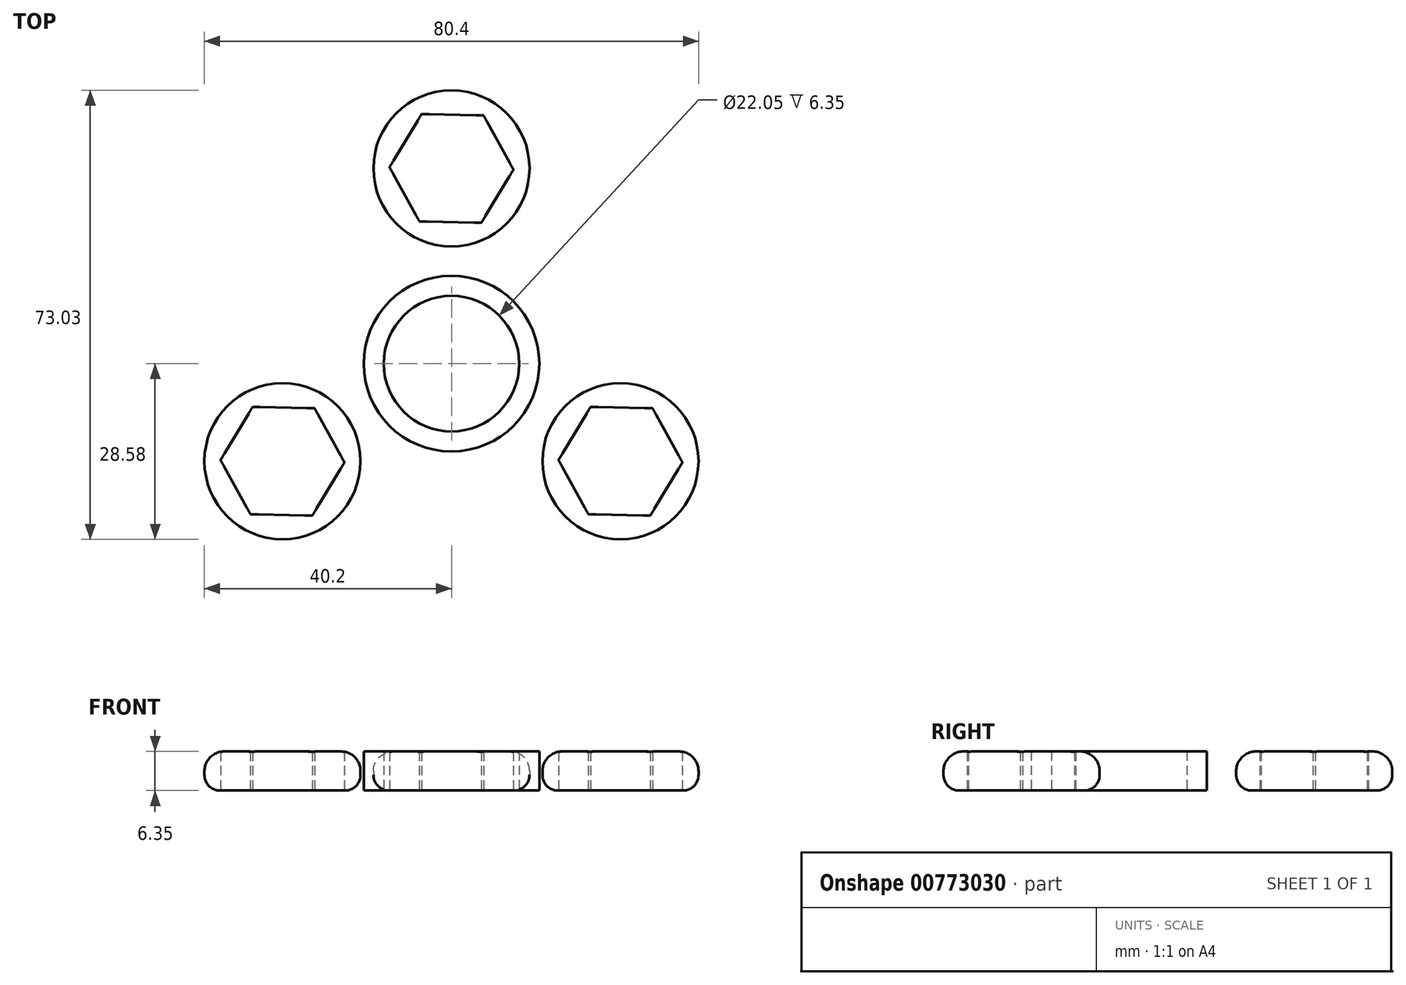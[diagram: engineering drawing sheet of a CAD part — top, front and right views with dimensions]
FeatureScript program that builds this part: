
annotation { "Feature Type Name" : "Feature", "Feature Type Description" : "" }
export const myFeature = defineFeature(function(context is Context, id is Id, definition is map)
    precondition{}
    {
        {
            var Q0;
            Q0=qCreatedBy(makeId("Top.planeOp"),FACE);
            var sketch = newSketch(context, id + "F0", { "sketchPlane" : qUnion([Q0])});
            skCircle(sketch, "E0", {"center": v(0, 0) * mm, "radius": 14.29 * mm});
            skCircle(sketch, "E1", {"center": v(0, 0) * mm, "radius": 11.02 * mm});
            skCircle(sketch, "E2.cCircle", {"center": v(0, 31.75) * mm, "radius": 8.73 * mm, "construction": true});
            skLineSegment(sketch, "E2.0", {"start": v(5.2, 40.38) * mm, "end": v(10.08, 31.55) * mm});
            skLineSegment(sketch, "E2.1", {"start": v(10.08, 31.55) * mm, "end": v(4.87, 22.92) * mm});
            skLineSegment(sketch, "E2.2", {"start": v(4.87, 22.92) * mm, "end": v(-5.2, 23.12) * mm});
            skLineSegment(sketch, "E2.3", {"start": v(-5.2, 23.12) * mm, "end": v(-10.08, 31.95) * mm});
            skLineSegment(sketch, "E2.4", {"start": v(-10.08, 31.95) * mm, "end": v(-4.87, 40.58) * mm});
            skLineSegment(sketch, "E2.5", {"start": v(-4.87, 40.58) * mm, "end": v(5.2, 40.38) * mm});
            skPoint(sketch, "E2.0.midPoint", {"position": v(7.64, 35.97) * mm});
            skCircle(sketch, "E3", {"center": v(0, 31.75) * mm, "radius": 12.7 * mm});
            skCircle(sketch, "E4.1.0", {"center": v(-27.5, -15.87) * mm, "radius": 8.73 * mm, "construction": true});
            skLineSegment(sketch, "E4.1.1", {"start": v(-22.29, -7.24) * mm, "end": v(-17.42, -16.07) * mm});
            skCircle(sketch, "E4.1.2", {"center": v(-27.5, -15.87) * mm, "radius": 12.7 * mm});
            skPoint(sketch, "E4.1.3", {"position": v(-34.97, -11.36) * mm});
            skLineSegment(sketch, "E4.1.4", {"start": v(-32.37, -7.05) * mm, "end": v(-22.29, -7.24) * mm});
            skLineSegment(sketch, "E4.1.5", {"start": v(-17.42, -16.07) * mm, "end": v(-22.63, -24.7) * mm});
            skLineSegment(sketch, "E4.1.6", {"start": v(-32.7, -24.5) * mm, "end": v(-37.58, -15.68) * mm});
            skLineSegment(sketch, "E4.1.7", {"start": v(-37.58, -15.68) * mm, "end": v(-32.37, -7.05) * mm});
            skLineSegment(sketch, "E4.1.8", {"start": v(-22.63, -24.7) * mm, "end": v(-32.7, -24.5) * mm});
            skCircle(sketch, "E4.2.0", {"center": v(27.5, -15.87) * mm, "radius": 8.73 * mm, "construction": true});
            skLineSegment(sketch, "E4.2.1", {"start": v(17.42, -15.68) * mm, "end": v(22.63, -7.05) * mm});
            skCircle(sketch, "E4.2.2", {"center": v(27.5, -15.87) * mm, "radius": 12.7 * mm});
            skPoint(sketch, "E4.2.3", {"position": v(27.33, -24.6) * mm});
            skLineSegment(sketch, "E4.2.4", {"start": v(22.29, -24.5) * mm, "end": v(17.42, -15.68) * mm});
            skLineSegment(sketch, "E4.2.5", {"start": v(22.63, -7.05) * mm, "end": v(32.7, -7.24) * mm});
            skLineSegment(sketch, "E4.2.6", {"start": v(37.58, -16.07) * mm, "end": v(32.37, -24.7) * mm});
            skLineSegment(sketch, "E4.2.7", {"start": v(32.37, -24.7) * mm, "end": v(22.29, -24.5) * mm});
            skLineSegment(sketch, "E4.2.8", {"start": v(32.7, -7.24) * mm, "end": v(37.58, -16.07) * mm});
            skSolve(sketch);
        }
        {
            var Q0;
            Q0=qCreatedBy(makeId("Top.planeOp"),FACE);
            var sketch = newSketch(context, id + "F1", { "sketchPlane" : qUnion([Q0])});
            skCircle(sketch, "E5.0", {"center": v(27.5, -15.87) * mm, "radius": 8.73 * mm});
            skCircle(sketch, "E5.1", {"center": v(27.5, -15.87) * mm, "radius": 12.7 * mm});
            skLineSegment(sketch, "E5.2", {"start": v(22.63, -7.05) * mm, "end": v(32.7, -7.24) * mm});
            skLineSegment(sketch, "E5.3", {"start": v(37.58, -16.07) * mm, "end": v(32.37, -24.7) * mm});
            skLineSegment(sketch, "E5.4", {"start": v(32.7, -7.24) * mm, "end": v(37.58, -16.07) * mm});
            skLineSegment(sketch, "E5.5", {"start": v(-22.29, -7.24) * mm, "end": v(-17.42, -16.07) * mm});
            skCircle(sketch, "E5.6", {"center": v(0, 31.75) * mm, "radius": 12.7 * mm});
            skLineSegment(sketch, "E5.7", {"start": v(-4.87, 40.58) * mm, "end": v(5.2, 40.38) * mm});
            skLineSegment(sketch, "E5.8", {"start": v(-10.08, 31.95) * mm, "end": v(-4.87, 40.58) * mm});
            skLineSegment(sketch, "E5.9", {"start": v(-5.2, 23.12) * mm, "end": v(-10.08, 31.95) * mm});
            skLineSegment(sketch, "E5.10", {"start": v(4.87, 22.92) * mm, "end": v(-5.2, 23.12) * mm});
            skLineSegment(sketch, "E5.11", {"start": v(10.08, 31.55) * mm, "end": v(4.87, 22.92) * mm});
            skCircle(sketch, "E5.12", {"center": v(0, 31.75) * mm, "radius": 8.73 * mm});
            skCircle(sketch, "E5.13", {"center": v(0, 0) * mm, "radius": 11.02 * mm});
            skCircle(sketch, "E5.14", {"center": v(0, 0) * mm, "radius": 14.29 * mm});
            skLineSegment(sketch, "E5.15", {"start": v(-17.42, -16.07) * mm, "end": v(-22.63, -24.7) * mm});
            skLineSegment(sketch, "E5.16", {"start": v(-22.63, -24.7) * mm, "end": v(-32.7, -24.5) * mm});
            skLineSegment(sketch, "E5.17", {"start": v(-32.37, -7.05) * mm, "end": v(-22.29, -7.24) * mm});
            skLineSegment(sketch, "E5.18", {"start": v(17.42, -15.68) * mm, "end": v(22.63, -7.05) * mm});
            skLineSegment(sketch, "E5.19", {"start": v(22.29, -24.5) * mm, "end": v(17.42, -15.68) * mm});
            skLineSegment(sketch, "E5.20", {"start": v(5.2, 40.38) * mm, "end": v(10.08, 31.55) * mm});
            skCircle(sketch, "E6.0", {"center": v(-27.5, -15.87) * mm, "radius": 12.7 * mm});
            skLineSegment(sketch, "E6.1", {"start": v(-32.7, -24.5) * mm, "end": v(-37.58, -15.68) * mm});
            skCircle(sketch, "E6.8", {"center": v(-27.5, -15.87) * mm, "radius": 8.73 * mm});
            skLineSegment(sketch, "E6.23", {"start": v(32.37, -24.7) * mm, "end": v(22.29, -24.5) * mm});
            skSolve(sketch);
        }
        {
            var Q0;
            Q0=qCreatedBy(makeId("Top.planeOp"),FACE);
            var sketch = newSketch(context, id + "F2", { "sketchPlane" : qUnion([Q0])});
            skArc(sketch, "E7.0", {"start": v(-24.29, -3.59) * mm, "mid": v(-38.47, -22.27) * mm, "end": v(-15.23, -19.15) * mm});
            skCircle(sketch, "E7.1", {"center": v(0, 31.75) * mm, "radius": 8.73 * mm});
            skArc(sketch, "E7.2", {"start": v(9.04, 22.83) * mm, "mid": v(-0.05, 44.45) * mm, "end": v(-8.97, 22.76) * mm});
            skArc(sketch, "E7.3", {"start": v(15.25, -19.24) * mm, "mid": v(38.52, -22.18) * mm, "end": v(24.2, -3.61) * mm});
            skCircle(sketch, "E7.4", {"center": v(27.5, -15.87) * mm, "radius": 8.73 * mm});
            skCircle(sketch, "E7.5", {"center": v(0, 0) * mm, "radius": 14.29 * mm});
            skCircle(sketch, "E7.6", {"center": v(0, 0) * mm, "radius": 11.02 * mm});
            skCircle(sketch, "E7.7", {"center": v(-27.5, -15.87) * mm, "radius": 8.73 * mm});
            skLineSegment(sketch, "E7.8", {"start": v(22.29, -24.5) * mm, "end": v(17.42, -15.68) * mm});
            skLineSegment(sketch, "E7.9", {"start": v(-37.58, -15.68) * mm, "end": v(-32.37, -7.05) * mm});
            skArc(sketch, "E7.10", {"start": v(-24.29, -3.59) * mm, "mid": v(-38.47, -22.27) * mm, "end": v(-15.23, -19.15) * mm});
            skCircle(sketch, "E7.11", {"center": v(-27.5, -15.87) * mm, "radius": 8.73 * mm});
            skLineSegment(sketch, "E7.12", {"start": v(-32.7, -24.5) * mm, "end": v(-37.58, -15.68) * mm});
            skCircle(sketch, "E7.13", {"center": v(0, 0) * mm, "radius": 11.02 * mm});
            skArc(sketch, "E7.14", {"start": v(9.04, 22.83) * mm, "mid": v(-0.05, 44.45) * mm, "end": v(-8.97, 22.76) * mm});
            skLineSegment(sketch, "E7.15", {"start": v(-22.29, -7.24) * mm, "end": v(-17.42, -16.07) * mm});
            skLineSegment(sketch, "E7.16", {"start": v(-32.37, -7.05) * mm, "end": v(-22.29, -7.24) * mm});
            skLineSegment(sketch, "E7.17", {"start": v(-22.63, -24.7) * mm, "end": v(-32.7, -24.5) * mm});
            skArc(sketch, "E7.18", {"start": v(15.25, -19.24) * mm, "mid": v(38.52, -22.18) * mm, "end": v(24.2, -3.61) * mm});
            skCircle(sketch, "E7.19", {"center": v(0, 31.75) * mm, "radius": 8.73 * mm});
            skLineSegment(sketch, "E7.20", {"start": v(-17.42, -16.07) * mm, "end": v(-22.63, -24.7) * mm});
            skCircle(sketch, "E7.21", {"center": v(27.5, -15.87) * mm, "radius": 8.73 * mm});
            skLineSegment(sketch, "E7.22", {"start": v(22.29, -24.5) * mm, "end": v(17.42, -15.68) * mm});
            skCircle(sketch, "E7.23", {"center": v(0, 0) * mm, "radius": 14.29 * mm});
            skCircle(sketch, "E7.24", {"center": v(27.5, -15.87) * mm, "radius": 8.73 * mm});
            skArc(sketch, "E7.25", {"start": v(15.25, -19.24) * mm, "mid": v(38.52, -22.18) * mm, "end": v(24.2, -3.61) * mm});
            skArc(sketch, "E7.26", {"start": v(9.04, 22.83) * mm, "mid": v(-0.05, 44.45) * mm, "end": v(-8.97, 22.76) * mm});
            skCircle(sketch, "E7.27", {"center": v(0, 31.75) * mm, "radius": 8.73 * mm});
            skCircle(sketch, "E7.28", {"center": v(0, 0) * mm, "radius": 11.02 * mm});
            skCircle(sketch, "E7.29", {"center": v(0, 0) * mm, "radius": 14.29 * mm});
            skLineSegment(sketch, "E7.30", {"start": v(32.37, -24.7) * mm, "end": v(22.29, -24.5) * mm});
            skLineSegment(sketch, "E7.31", {"start": v(37.58, -16.07) * mm, "end": v(32.37, -24.7) * mm});
            skLineSegment(sketch, "E7.32", {"start": v(17.42, -15.68) * mm, "end": v(22.63, -7.05) * mm});
            skLineSegment(sketch, "E7.33", {"start": v(10.08, 31.55) * mm, "end": v(4.87, 22.92) * mm});
            skLineSegment(sketch, "E7.34", {"start": v(4.87, 22.92) * mm, "end": v(-5.2, 23.12) * mm});
            skLineSegment(sketch, "E7.35", {"start": v(22.63, -7.05) * mm, "end": v(32.7, -7.24) * mm});
            skLineSegment(sketch, "E7.36", {"start": v(-5.2, 23.12) * mm, "end": v(-10.08, 31.95) * mm});
            skLineSegment(sketch, "E7.37", {"start": v(-10.08, 31.95) * mm, "end": v(-4.87, 40.58) * mm});
            skLineSegment(sketch, "E7.38", {"start": v(5.2, 40.38) * mm, "end": v(10.08, 31.55) * mm});
            skLineSegment(sketch, "E7.39", {"start": v(32.7, -7.24) * mm, "end": v(37.58, -16.07) * mm});
            skLineSegment(sketch, "E7.40", {"start": v(-4.87, 40.58) * mm, "end": v(5.2, 40.38) * mm});
            skArc(sketch, "E8", {"start": v(-32.37, -7.05) * mm, "mid": v(-13.14, 7.83) * mm, "end": v(-10.08, 31.95) * mm});
            skArc(sketch, "E9", {"start": v(10.08, 31.55) * mm, "mid": v(13.35, 7.47) * mm, "end": v(32.7, -7.24) * mm});
            skArc(sketch, "E10", {"start": v(22.29, -24.5) * mm, "mid": v(-0.21, -15.3) * mm, "end": v(-22.63, -24.7) * mm});
            skSolve(sketch);
        }
        {
            var Q0;
            Q0=makeQuery(id+"F1.imprint","IMPRINT",FACE,{"disambiguationData":[TD([[makeQuery(id+"F1.imprint","IMPRINT",EDGE,{"derivedFrom":sQuery(id+"F1.wireOp",EDGE,"E5.6")}),1.0]])]});
            var Q1;
            Q1=makeQuery(id+"F2.imprint","IMPRINT",FACE,{"disambiguationData":[TD([[makeQuery(id+"F2.imprint","IMPRINT",EDGE,{"derivedFrom":sQuery(id+"F2.wireOp",EDGE,"E7.29")}),-1.0]])]});
            var Q2;
            Q2=makeQuery(id+"F1.imprint","IMPRINT",FACE,{"disambiguationData":[TD([[makeQuery(id+"F1.imprint","IMPRINT",EDGE,{"derivedFrom":sQuery(id+"F1.wireOp",EDGE,"E5.1")}),1.0]])]});
            var Q3;
            Q3=makeQuery(id+"F0.imprint","IMPRINT",FACE,{"disambiguationData":[TD([[makeQuery(id+"F0.imprint","IMPRINT",EDGE,{"derivedFrom":sQuery(id+"F0.wireOp",EDGE,"E4.1.1")}),1.0]])]});
            var Q4;
            Q4=makeQuery(id+"F0.imprint","IMPRINT",FACE,{"disambiguationData":[TD([[makeQuery(id+"F0.imprint","IMPRINT",EDGE,{"derivedFrom":sQuery(id+"F0.wireOp",EDGE,"E0")}),1.0]])]});
            extrude(context, id + "F3", {"entities" : qUnion([Q0, Q1, Q2, Q3, Q4]), "depth" : 6.35 * mm, "offsetDistance" : 25.4 * mm});
        }
        {
            var Q0;
            Q0=makeQuery(id+"F3.opExtrude","CAP_EDGE",EDGE,{"disambiguationData":[OSD([sQuery(id+"F0.wireOp",EDGE,"E4.1.2")])],"isStart":true});
            var Q1;
            Q1=makeQuery(id+"F3.opExtrude","CAP_EDGE",EDGE,{"disambiguationData":[OSD([sQuery(id+"F2.wireOp",EDGE,"E8")])],"isStart":true});
            var Q2;
            Q2=makeQuery(id+"F3.opExtrude","CAP_EDGE",EDGE,{"disambiguationData":[OSD([sQuery(id+"F1.wireOp",EDGE,"E5.6")])],"isStart":true});
            var Q3;
            Q3=makeQuery(id+"F3.opExtrude","CAP_EDGE",EDGE,{"disambiguationData":[OSD([sQuery(id+"F2.wireOp",EDGE,"E9")])],"isStart":true});
            var Q4;
            Q4=makeQuery(id+"F3.opExtrude","CAP_EDGE",EDGE,{"disambiguationData":[OSD([sQuery(id+"F1.wireOp",EDGE,"E5.1")])],"isStart":true});
            var Q5;
            Q5=makeQuery(id+"F3.opExtrude","CAP_EDGE",EDGE,{"disambiguationData":[OSD([sQuery(id+"F2.wireOp",EDGE,"E10")])],"isStart":true});
            fillet(context, id + "F4", {"entities" : qUnion([Q0, Q1, Q2, Q3, Q4, Q5]), "radius" : 2.54 * mm, "tangentPropagation" : true, "allowEdgeOverflow" : false});
        }
        {
            var Q0;
            Q0=makeQuery(id+"F3.opExtrude","CAP_EDGE",EDGE,{"disambiguationData":[OSD([sQuery(id+"F2.wireOp",EDGE,"E8")])],"isStart":false});
            var Q1;
            Q1=makeQuery(id+"F3.opExtrude","CAP_EDGE",EDGE,{"disambiguationData":[OSD([sQuery(id+"F0.wireOp",EDGE,"E4.1.2")])],"isStart":false});
            var Q2;
            Q2=makeQuery(id+"F3.opExtrude","CAP_EDGE",EDGE,{"disambiguationData":[OSD([sQuery(id+"F2.wireOp",EDGE,"E10")])],"isStart":false});
            var Q3;
            Q3=makeQuery(id+"F3.opExtrude","CAP_EDGE",EDGE,{"disambiguationData":[OSD([sQuery(id+"F1.wireOp",EDGE,"E5.1")])],"isStart":false});
            var Q4;
            Q4=makeQuery(id+"F3.opExtrude","CAP_EDGE",EDGE,{"disambiguationData":[OSD([sQuery(id+"F2.wireOp",EDGE,"E9")])],"isStart":false});
            var Q5;
            Q5=makeQuery(id+"F3.opExtrude","CAP_EDGE",EDGE,{"disambiguationData":[OSD([sQuery(id+"F1.wireOp",EDGE,"E5.6")])],"isStart":false});
            fillet(context, id + "F5", {"entities" : qUnion([Q0, Q1, Q2, Q3, Q4, Q5]), "radius" : 3.17 * mm, "tangentPropagation" : true, "allowEdgeOverflow" : false});
        }
    });
